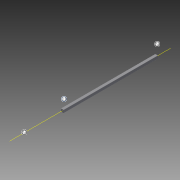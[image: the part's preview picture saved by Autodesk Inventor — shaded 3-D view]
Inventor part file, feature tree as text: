
AUTODESK INVENTOR PART (.ipt)
format: ipt  version: 2015 (Build 190159000, 159)  size: 157,184 bytes
history: native  units: in
note: dims shown in document units (in); Inventor stores cm internally (conversion verified against a paired STEP export)
features: other x6, extrude x1, imported_body x1, sketch x1
ambient origin geometry x8: Origin, YZ Plane, XZ Plane, XY Plane, X Axis, Y Axis, Z Axis, Center Point
bodies: Body1 (feature_tree)
feature tree (9):
  other  "Shaft 4.25 inch"
  parser-record x1  (decoder bookkeeping rows leaked as tree rows — omitted from the tree; the rows remain in map.json)
  other  "Shaft"
  extrude  "length cut"  Depth=4.25in
  other  "front plane"
  imported_body  "Base1"
  sketch  "Sketch1"  dims[d1=0.0in d2=4.25in d3=0.0in d4=0.0in d5=0.0in]
  other  "main axis"
  other  "back plane"
